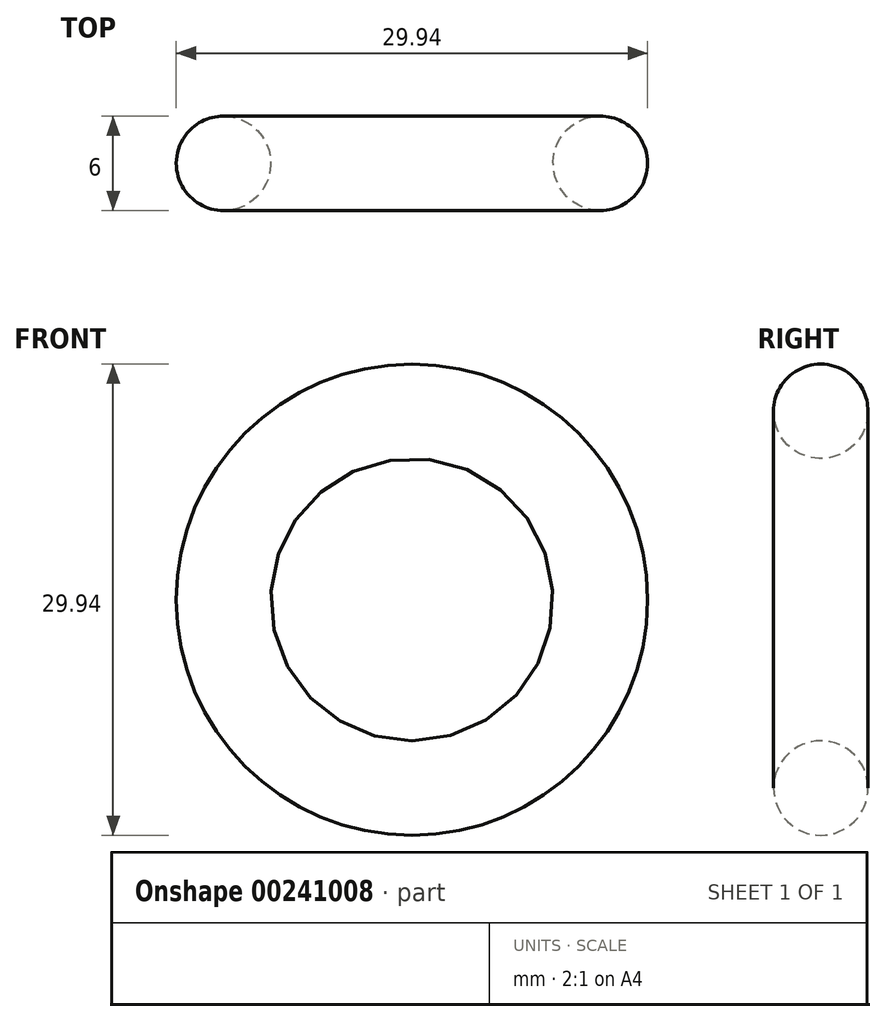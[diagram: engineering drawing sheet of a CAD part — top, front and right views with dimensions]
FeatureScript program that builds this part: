
annotation { "Feature Type Name" : "Feature", "Feature Type Description" : "" }
export const myFeature = defineFeature(function(context is Context, id is Id, definition is map)
    precondition{}
    {
        {
            var Q0;
            Q0=qCreatedBy(makeId("Right.planeOp"),FACE);
            var sketch = newSketch(context, id + "F0", { "sketchPlane" : qUnion([Q0])});
            skCircle(sketch, "E0", {"center": v(0, 39.89) * mm, "radius": 10 * mm});
            skSolve(sketch);
        }
        {
            var Q0;
            Q0=qCreatedBy(makeId("Front.planeOp"),FACE);
            var sketch = newSketch(context, id + "F1", { "sketchPlane" : qUnion([Q0])});
            skLineSegment(sketch, "E1.0.0", {"start": v(0, 49.89) * mm, "end": v(0, 29.89) * mm});
            skCircle(sketch, "E2", {"center": v(0, 0) * mm, "radius": 29.89 * mm});
            skSolve(sketch);
        }
        {
            var Q0;
            Q0=makeQuery(id+"F0.imprint","IMPRINT",FACE,{"disambiguationData":[TD([[makeQuery(id+"F0.imprint","IMPRINT",EDGE,{"derivedFrom":sQuery(id+"F0.wireOp",EDGE,"E0")}),1.0]])]});
            var Q1;
            Q1=sQuery(id+"F1.wireOp",EDGE,"E2");
            sweep(context, id + "F2", {"profiles" : qUnion([Q0]), "path" : qUnion([Q1])});
        }
        {
            var Q0;
            Q0=makeQuery(id+"F2.opSweep","SWEPT_BODY",BODY,{"disambiguationData":[OSD([sQuery(id+"F0.wireOp",EDGE,"E0"),sQuery(id+"F1.wireOp",EDGE,"E2")])]});
            var Q1;
            Q1=sQuery(id+"F1.wireOp",VERTEX,"E2.center");
            transform(context, id + "F3", {"entities" : qUnion([Q0]), "transformType" : TransformType.SCALE_UNIFORMLY, "scale" : 0.3, "scalePoint" : qUnion([Q1]), "makeCopy" : false});
        }
    });
